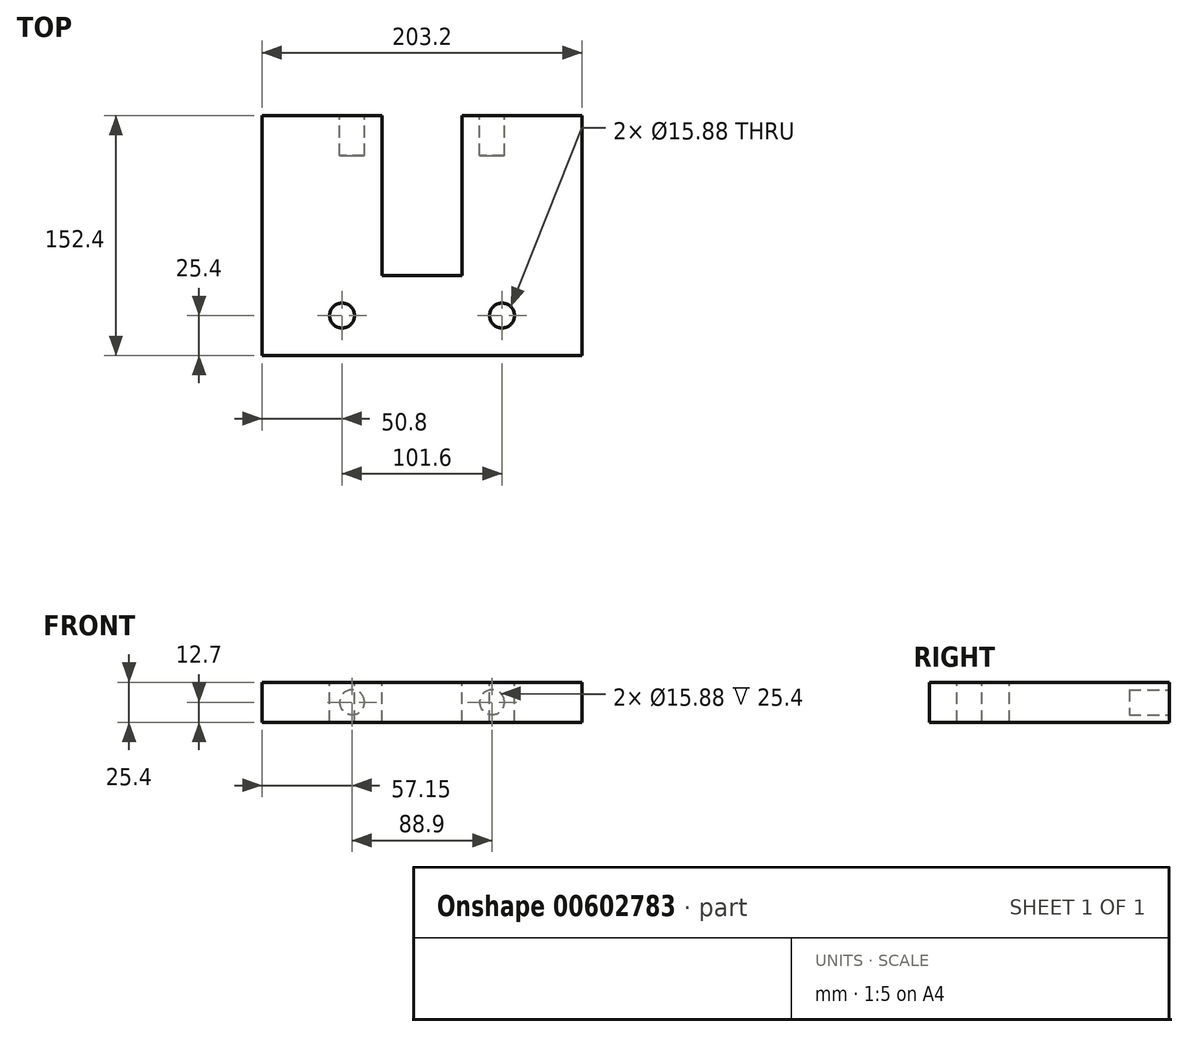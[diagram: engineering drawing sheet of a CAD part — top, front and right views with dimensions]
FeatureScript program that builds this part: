
annotation { "Feature Type Name" : "Feature", "Feature Type Description" : "" }
export const myFeature = defineFeature(function(context is Context, id is Id, definition is map)
    precondition{}
    {
        {
            var Q0;
            Q0=qCreatedBy(makeId("Top.planeOp"),FACE);
            var sketch = newSketch(context, id + "F0", { "sketchPlane" : qUnion([Q0])});
            skLineSegment(sketch, "E0.bottom", {"start": v(101.6, -76.2) * mm, "end": v(-101.6, -76.2) * mm});
            skLineSegment(sketch, "E0.top", {"start": v(101.6, 76.2) * mm, "end": v(-101.6, 76.2) * mm});
            skLineSegment(sketch, "E0.left", {"start": v(101.6, -76.2) * mm, "end": v(101.6, 76.2) * mm});
            skLineSegment(sketch, "E0.right", {"start": v(-101.6, -76.2) * mm, "end": v(-101.6, 76.2) * mm});
            skPoint(sketch, "E0.middle", {"position": v(0, 0) * mm});
            skCircle(sketch, "E1", {"center": v(0, 0) * mm, "radius": 7.94 * mm});
            skSolve(sketch);
        }
        {
            var Q0;
            Q0=makeQuery(id+"F0.imprint","IMPRINT",FACE,{"disambiguationData":[TD([[makeQuery(id+"F0.imprint","IMPRINT",EDGE,{"derivedFrom":sQuery(id+"F0.wireOp",EDGE,"E0.bottom")}),-1.0]])]});
            extrude(context, id + "F1", {"entities" : qUnion([Q0]), "depth" : 25.4 * mm, "offsetDistance" : 25.4 * mm});
        }
        {
            var Q0;
            Q0=makeQuery(id+"F1.opExtrude","CAP_FACE",FACE,{"disambiguationData":[OSD([sQuery(id+"F0.wireOp",EDGE,"E0.bottom"),sQuery(id+"F0.wireOp",EDGE,"E0.top"),sQuery(id+"F0.wireOp",EDGE,"E0.left"),sQuery(id+"F0.wireOp",EDGE,"E0.right"),sQuery(id+"F0.wireOp",EDGE,"E1")])],"isStart":false});
            var sketch = newSketch(context, id + "F2", { "sketchPlane" : qUnion([Q0])});
            skLineSegment(sketch, "E2", {"start": v(0, 205.8) * mm, "end": v(0, -227) * mm, "construction": true});
            skPoint(sketch, "E2.startSnap0", {"position": v(0, 76.2) * mm});
            skLineSegment(sketch, "E3", {"start": v(-209.33, 0) * mm, "end": v(193.77, 0) * mm, "construction": true});
            skPoint(sketch, "E3.endSnap0", {"position": v(-101.6, 0) * mm});
            skLineSegment(sketch, "E4.bottom", {"start": v(25.4, -25.4) * mm, "end": v(-25.4, -25.4) * mm});
            skLineSegment(sketch, "E4.top", {"start": v(25.4, 177.8) * mm, "end": v(-25.4, 177.8) * mm});
            skLineSegment(sketch, "E4.left", {"start": v(25.4, -25.4) * mm, "end": v(25.4, 177.8) * mm});
            skLineSegment(sketch, "E4.right", {"start": v(-25.4, -25.4) * mm, "end": v(-25.4, 177.8) * mm});
            skSolve(sketch);
        }
        {
            var Q0;
            Q0 = qSketchRegion(id + "F2", true);
            extrude(context, id + "F3", {"entities" : qUnion([Q0]), "operationType" : NewBodyOperationType.REMOVE, "oppositeDirection" : true, "depth" : 50.8 * mm, "offsetDistance" : 25.4 * mm});
        }
        {
            var Q0;
            {var subQ1=sQuery(id+"F2.wireOp",EDGE,"E4.bottom");Q0=makeQuery(id+"F2.imprint","IMPRINT",FACE,{"disambiguationData":[TD([[makeQuery(id+"F2.imprint","IMPRINT",EDGE,{"derivedFrom":subQ1}),1.0]])]});}
            var sketch = newSketch(context, id + "F4", { "sketchPlane" : qUnion([Q0])});
            skCircle(sketch, "E5", {"center": v(-50.8, -50.8) * mm, "radius": 7.94 * mm});
            skCircle(sketch, "E6", {"center": v(50.8, -50.8) * mm, "radius": 7.94 * mm});
            skSolve(sketch);
        }
        {
            var Q0;
            Q0 = qSketchRegion(id + "F4", true);
            extrude(context, id + "F5", {"entities" : qUnion([Q0]), "operationType" : NewBodyOperationType.REMOVE, "oppositeDirection" : true, "depth" : 25.4 * mm, "offsetDistance" : 25.4 * mm});
        }
        {
            var Q0;
            {var subQ2=sQuery(id+"F0.wireOp",EDGE,"E0.left");var subQ3=sQuery(id+"F0.wireOp",EDGE,"E0.top");Q0=makeQuery(id+"F3.boolean.opBoolean","SPLIT",FACE,{"disambiguationData":[TD([makeQuery(id+"F1.opExtrude","SWEPT_FACE",FACE,{"disambiguationData":[OSD([subQ2])]})])],"derivedFrom":makeQuery(id+"F1.opExtrude","SWEPT_FACE",FACE,{"disambiguationData":[OSD([subQ3])]})});}
            var sketch = newSketch(context, id + "F6", { "sketchPlane" : qUnion([Q0])});
            skCircle(sketch, "E7", {"center": v(-44.45, 12.7) * mm, "radius": 7.94 * mm});
            skPoint(sketch, "E7.centerSnap0", {"position": v(-25.4, 12.7) * mm});
            skCircle(sketch, "E8.MirrorC", {"center": v(44.45, 12.7) * mm, "radius": 7.94 * mm});
            skSolve(sketch);
        }
        {
            var Q0;
            Q0 = qSketchRegion(id + "F6", true);
            extrude(context, id + "F7", {"entities" : qUnion([Q0]), "operationType" : NewBodyOperationType.REMOVE, "oppositeDirection" : true, "depth" : 25.4 * mm, "offsetDistance" : 25.4 * mm});
        }
    });
